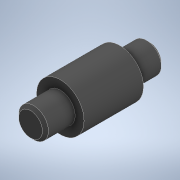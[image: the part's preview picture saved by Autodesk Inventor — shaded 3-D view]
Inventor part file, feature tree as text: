
AUTODESK INVENTOR PART (.ipt)
format: ipt  version: 2022 (Build 260153000, 153)  size: 114,176 bytes
history: native  units: mm
features: extrude x2, sketch x2, chamfer x1
ambient origin geometry x8: Origin, YZ Plane, XZ Plane, XY Plane, X Axis, Y Axis, Z Axis, Center Point
bodies: Solid1 (feature_tree)
feature tree (5):
  extrude  "Extrusion1"  Depth=20.0mm TaperAngle=0.0deg
  chamfer  "Chamfer1"  Distance=0.5mm Angle=45.0deg
  extrude  "Extrusion2"  Depth=10.0mm TaperAngle=0.0deg
  sketch  "Sketch1"  dims[d0=5.0mm d1=20.0mm d2=0.0mm d3=0.5mm d4=2.0mm d5=45.0deg]
  sketch  "Sketch2"  dims[d6=8.0mm d7=10.0mm d8=0.0mm]
